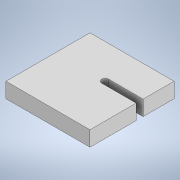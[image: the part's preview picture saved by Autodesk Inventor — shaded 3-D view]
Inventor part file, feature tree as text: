
AUTODESK INVENTOR PART (.ipt)
format: ipt  version: 2020 (Build 240168000, 168)  size: 96,768 bytes
history: native  units: mm
features: extrude x1, sketch x1
ambient origin geometry x8: Origin, YZ Plane, XZ Plane, XY Plane, X Axis, Y Axis, Z Axis, Center Point
bodies: Solide1 (feature_tree)
feature tree (2):
  extrude  "Extrusion1"  Depth=122.0mm
  sketch  "Esquisse1"
